# Revit family: WashBasin-40cm-SquareBowl-VitrA-WaterJewelsSeries-4441B003-1361
name_source: partatom
category: Generic Models
revit_build: Autodesk Revit 2017 (Build: 20160225_1515(x64)
units: mm (PartAtom-declared; Revit-internal decimal feet)

## family parameters
Always vertical = Yes
Can host rebar = No
Cut with Voids When Loaded = No
OmniClass Number = 23.45.05.14.14
OmniClass Title = Sinks/Lavatories
Part Type = Normal
Room Calculation Point = No
Round Connector Dimension = Use Diameter
Shared = Yes
Work Plane-Based = No

## types (4) — shared parameters
BIMobject category = Sanitary - Basins
Brand = VitrA
CW Connection = No
Default Elevation = 850
Description = WAter Jewels Bowl, Without Tap Hole, Without Overflow Hole, 40 cm
Design country = Turkey
HW Connection = No
IFC Classification = Sanitary Terminal
Manufacturer = Vitra
Manufacturer name = Vitra
Masterformat 2014 Code = 22 41 16
Masterformat 2014 Description = Residential Lavatories and Sinks
MountingType = Countertop
NBS Referans Code = 35-65-70-94
NBS Referans Description = Wash Basin Systems
NominalDepth = 400 mm  [stored 1.31234 ft]
NominalHeight = 150 mm
NominalWidth = 400 mm  [stored 1.31234 ft]
OmniClass Code = 23.45.05.14.14
OmniClass Description = Sinks/Lavatories
Product Manual = Without Tap Hole, Without Overflow Hole, 40 cm
Product certification = https://vitraglobal.com
Product data url = https://www.vitraglobal.com
Product family = İstanbul Bowl
Product group = Square Bowls
Secondary Material = <By Category>
Technical description = https://www.vitraglobal.com
UNSPSC Code = 301815
URL = https://vitraglobal.com
Uniclass 1.4 Code = L7212
Uniclass 1.4 Description = Washbasins
Uniclass 2.0 Code = SS-35-65-70-94
Uniclass 2.0 Description = Sanitary Dispensing And Disposal Units
Uniclass 2015 Code = Pr_40_20_96_81
Uniclass 2015 Name = Wash basins, Sinks and troughs
Uniformat II Code = D2010
Uniformat II Description = Plumbing Fixtures
Vent Connection = No
Warranty Period (Year) = 10
Waste Connection = Yes
Weight Net (kg) = 7,797
Youtube = https://www.youtube.com
zero-valued in all types: Cost

## per-type parameters (varying)
| type | Article No. (default) | Color | Main Material | Model | Product SKU |
| WashBasin-40cm-SquareBowl-VitrA-WaterJewelsSeries-4441B003-1361 | 4441B003-1361 | White | Ceramic-White | 4441B003-1361 | 4441B003-1361 |
| WashBasin-40cm-SquareBowl-VitrA-WaterJewelsSeries-4441B071-0061 | 4441B071-0016 | Platinum | Platin-Ceramic | 4441B071-0016 | 4441B071-0016 |
| WashBasin-40cm-SquareBowl-VitrA-WaterJewelsSeries-4441B072-0016 | 4441B072-0016 | Gold | Gold-Ceramic | 4441B072-0016 | 4441B072-0016 |
| WashBasin-40cm-SquareBowl-VitrA-WaterJewelsSeries-4441B073-0016 | 4441B073-0016 | Copper | Copper-Ceramic | 4441B073-0016 | 4441B073-0016 |

note: [stored X ft] marks values corroborated as IEEE doubles in the binary element streams (Revit-internal decimal feet)

## geometry (parser evidence)
native form markers: Sweep x3
no freeform markers — native parametric forms only
